# Revit family: Toilet-Floor_Mount-KOHLER-Cavata-K-76977_1
name_source: partatom
category: Plumbing Fixtures
units: mm (PartAtom-declared; Revit-internal decimal feet)

## family parameters
Cut with Voids When Loaded = No
Host = Face
OmniClass Number = 23.31.19.00
OmniClass Title = Toilets
Part Type = Normal
Room Calculation Point = No
Round Connector Dimension = Use Diameter
Shared = No

## types (1)
- 0-White
    ADA Compliant = Yes
    Assembly Code = D2010100
    Bowl Height = 16 1/2"
    CW Connection = Yes
    Cold Water Inlet = Cold Water Inlet
    Date Modified = 05/13/2023
    Default Elevation = 0"
    Description = The Complete Solution Two Piece Round Front Toilet, 1.28 GPF
    Finish = Kohler-Vitreous_China-0-White
    Flow Rate = 0 GPM
    Flush Rate- GPF = 1.28 GPF
    Flush Rate- LPF = 4.8 LPF
    HW Connection = No
    Height = 30 9/16"
    Hot Water Inlet = Hot Water Inlet
    Length = 27 5/8"
    Manufacturer = Kohler Co.
    Master Format 2014 = 22 42 13.13
    Master Format 2014 Name = Residential Water Closets
    Material = Vitreous China
    Model = K-76977-0
    Pressure = 0.00 psi
    Product Documentation Link = https://www.us.kohler.com
    Product Name = Cavata
    Product Page URL = http://www.us.kohler.com
    Rough-In = 12"
    Seat Included = Yes
    Type = 1
    URL = https://www.us.kohler.com
    Vent Connection = No
    Waste Connection = Yes
    Waste Water Outlet = Waste Water Outlet
    WaterSense Certified = Yes
    Width = 19 5/8"

## geometry (parser evidence)
native form markers: Sweep x5
no freeform markers — native parametric forms only
